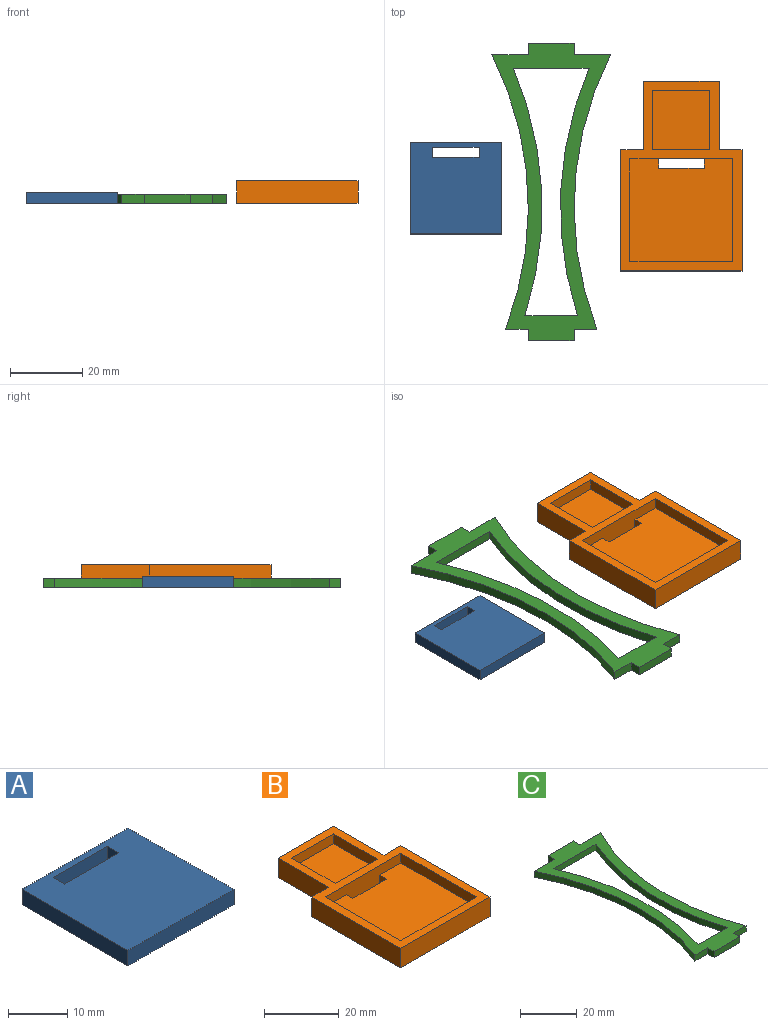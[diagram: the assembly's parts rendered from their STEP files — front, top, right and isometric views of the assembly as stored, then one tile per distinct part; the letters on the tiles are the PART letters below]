
ASSEMBLY  parts=3 mates=2
PART A: 10 faces, bbox 25.4x25.4x3.2 mm
  f0: plane 25.4x3.18mm, normal (-1,0,0), area 80.6mm2, adj f1,f3,f4,f5
  f1: plane 25.4x3.18mm, normal (0,-1,0), area 80.6mm2, adj f0,f2,f4,f5
  f2: plane 25.4x3.18mm, normal (1,0,0), area 80.6mm2, adj f1,f3,f4,f5
  f3: plane 25.4x3.18mm, normal (0,1,0), area 80.6mm2, adj f0,f2,f4,f5
  f4: plane 25.4x25.4mm, normal (0,0,1), area 609mm2, adj f0,f1,f2,f3,f6,f7,f8,f9
  f5: plane 25.4x25.4mm, normal (0,0,-1), area 609mm2, adj f0,f1,f2,f3,f6,f7,f8,f9
  f6: plane 3.18x2.79mm, normal (1,0,0), area 8.9mm2, adj f4,f5,f7,f9
  f7: plane 12.95x3.18mm, normal (0,1,0), area 41.1mm2, adj f4,f5,f6,f8
  f8: plane 3.18x2.79mm, normal (-1,0,0), area 8.9mm2, adj f4,f5,f7,f9
  f9: plane 12.95x3.18mm, normal (0,-1,0), area 41.1mm2, adj f4,f5,f6,f8
PART B: 23 faces, bbox 33.7x52.7x6.4 mm
  f0: plane 28.58x28.58mm, normal (0,0,1), area 784.3mm2, adj f3,f7,f8,f9,f20,f21,f22
  f1: plane 52.71x33.66mm, normal (0,0,-1), area 1499.6mm2, adj f3,f10,f11,f12,f13,f14,f15,f16
  f2: plane 16.51x15.88mm, normal (0,0,1), area 262.1mm2, adj f4,f5,f6,f19
  f3: plane 28.58x6.35mm, normal (0,-1,0), area 131mm2, adj f0,f1,f7,f9,f18,f20,f21
  f4: plane 16.51x3.18mm, normal (-1,0,0), area 52.4mm2, adj f2,f5,f18,f19
  f5: plane 15.88x3.18mm, normal (0,-1,0), area 50.4mm2, adj f2,f4,f6,f18
  f6: plane 16.51x3.18mm, normal (1,0,0), area 52.4mm2, adj f2,f5,f18,f19
  f7: plane 28.58x3.18mm, normal (1,0,0), area 90.7mm2, adj f0,f3,f8,f18
  f8: plane 28.58x3.18mm, normal (0,1,0), area 90.7mm2, adj f0,f7,f9,f18
  f9: plane 28.58x3.18mm, normal (-1,0,0), area 90.7mm2, adj f0,f3,f8,f18
  f10: plane 6.35x6.35mm, normal (0,1,0), area 40.3mm2, adj f1,f11,f17,f18
  f11: plane 19.05x6.35mm, normal (-1,0,0), area 121mm2, adj f1,f10,f12,f18
  f12: plane 20.96x6.35mm, normal (0,1,0), area 133.1mm2, adj f1,f11,f13,f18
  f13: plane 19.05x6.35mm, normal (1,0,0), area 121mm2, adj f1,f12,f14,f18
  f14: plane 6.35x6.35mm, normal (0,1,0), area 40.3mm2, adj f1,f13,f15,f18
  f15: plane 33.66x6.35mm, normal (1,0,0), area 213.7mm2, adj f1,f14,f16,f18
  f16: plane 33.66x6.35mm, normal (0,-1,0), area 213.7mm2, adj f1,f15,f17,f18
  f17: plane 33.66x6.35mm, normal (-1,0,0), area 213.7mm2, adj f1,f10,f16,f18
  f18: plane 52.71x33.66mm, normal (0,0,1), area 453.2mm2, adj f3,f4,f5,f6,f7,f8,f9,f10
  f19: plane 15.88x3.18mm, normal (0,1,0), area 50.4mm2, adj f2,f4,f6,f18
  f20: plane 3.18x2.54mm, normal (-1,0,0), area 8.1mm2, adj f0,f1,f3,f22
  f21: plane 3.18x2.54mm, normal (1,0,0), area 8.1mm2, adj f0,f1,f3,f22
  f22: plane 12.7x3.18mm, normal (0,1,0), area 40.3mm2, adj f0,f1,f20,f21
PART C: 18 faces, bbox 33x82.6x2.5 mm
  f0: plane 10.16x2.54mm, normal (0,1,0), area 25.8mm2, adj f1,f11,f12,f13
  f1: plane 3.18x2.54mm, normal (1,0,0), area 8.1mm2, adj f0,f2,f12,f13
  f2: plane 12.7x2.54mm, normal (0,1,0), area 32.3mm2, adj f1,f3,f12,f13
  f3: plane 3.18x2.54mm, normal (-1,0,0), area 8.1mm2, adj f2,f4,f12,f13
  f4: plane 10.16x2.54mm, normal (0,1,0), area 25.8mm2, adj f3,f5,f12,f13
  f5: cylinder r=93.37mm len=76.2mm, axis (0,0,-1), area 199.6mm2, adj f4,f6,f12,f13
  f6: plane 6.35x2.54mm, normal (0,-1,0), area 16.1mm2, adj f5,f7,f12,f13
  f7: plane 3.18x2.54mm, normal (-1,0,0), area 8.1mm2, adj f6,f8,f12,f13
  f8: plane 12.7x2.54mm, normal (0,-1,0), area 32.3mm2, adj f7,f9,f12,f13
  f9: plane 3.18x2.54mm, normal (1,0,0), area 8.1mm2, adj f8,f10,f12,f13
  f10: plane 6.35x2.54mm, normal (0,-1,0), area 16.1mm2, adj f9,f11,f12,f13
  f11: cylinder r=93.37mm len=76.2mm, axis (0,0,-1), area 199.6mm2, adj f0,f10,f12,f13
  f12: plane 82.55x33.02mm, normal (0,0,1), area 825.9mm2, adj f0,f1,f2,f3,f4,f5,f6,f7
  f13: plane 82.55x33.02mm, normal (0,0,-1), area 825.9mm2, adj f0,f1,f2,f3,f4,f5,f6,f7
  f14: cylinder r=97.18mm len=68.58mm, axis (0,0,1), area 178.2mm2, adj f12,f13,f15,f16
  f15: plane 14.6x2.54mm, normal (0,1,0), area 37.1mm2, adj f12,f13,f14,f17
  f16: plane 21.02x2.54mm, normal (0,-1,0), area 53.4mm2, adj f12,f13,f14,f17
  f17: cylinder r=97.18mm len=68.58mm, axis (0,0,1), area 178.2mm2, adj f12,f13,f15,f16
PLACE A t=(-20.86,0.82,2.3)mm
PLACE B t=(41.78,-5.32,2.3)mm
PLACE C t=(5.64,-0.22,2.3)mm
MATE planar C.f13 <-> B.f1  axis (0,0,-1) through (5.64,1.11,2.3)mm
MATE planar A.f5 <-> C.f13  axis (0,0,-1) through (-20.86,0.23,2.3)mm
